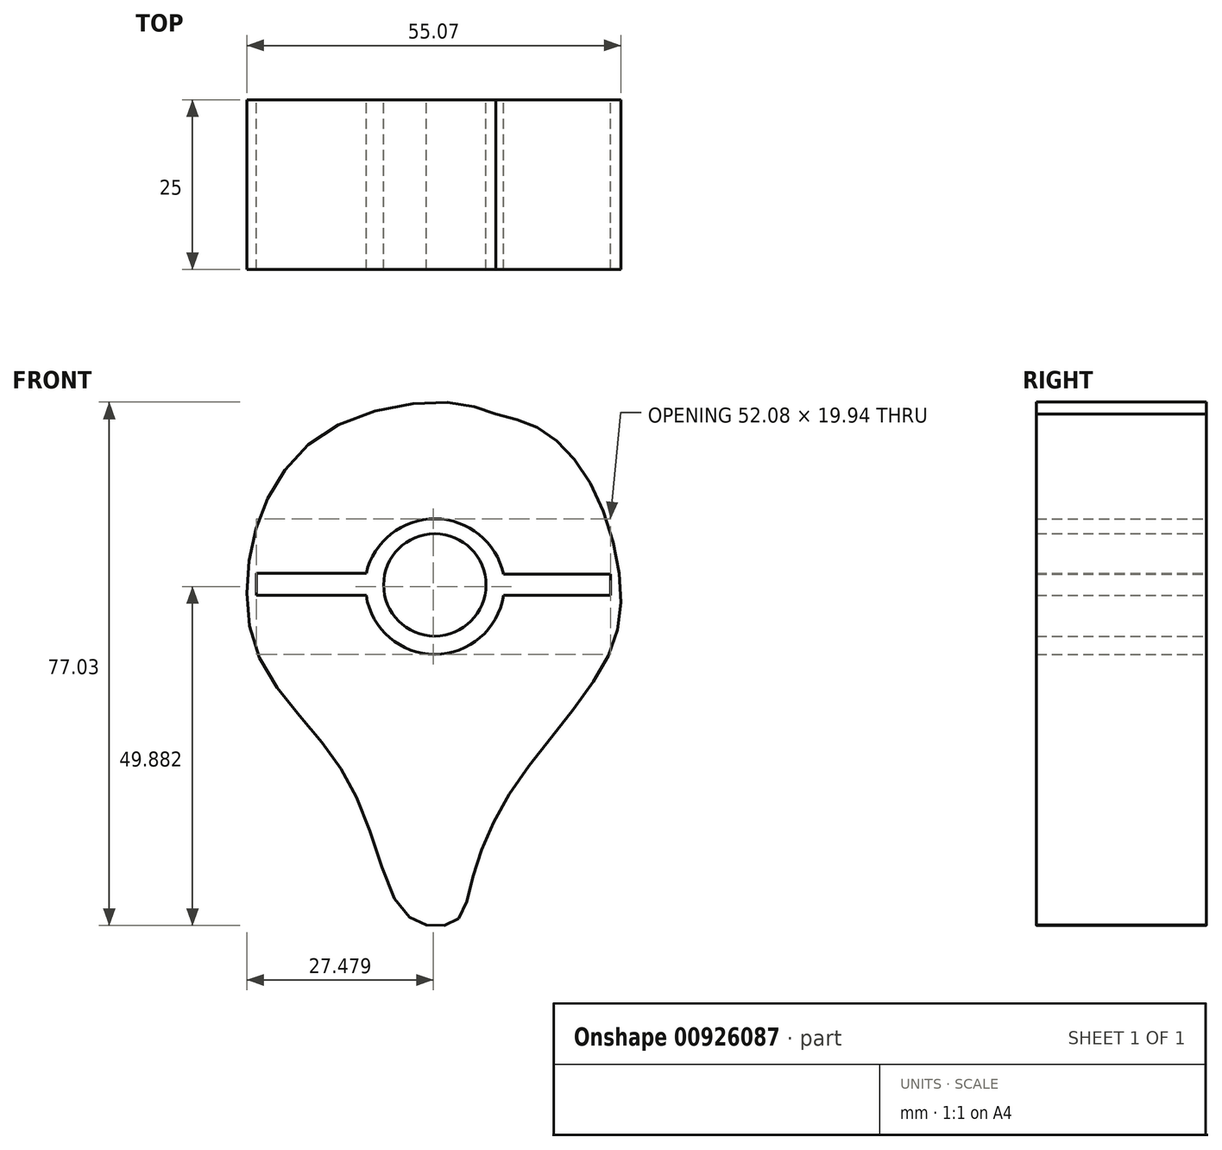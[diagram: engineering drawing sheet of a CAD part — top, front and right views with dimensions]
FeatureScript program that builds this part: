
annotation { "Feature Type Name" : "Feature", "Feature Type Description" : "" }
export const myFeature = defineFeature(function(context is Context, id is Id, definition is map)
    precondition{}
    {
        {
            var Q0;
            Q0=qCreatedBy(makeId("Front.planeOp"),FACE);
            var sketch = newSketch(context, id + "F0", { "sketchPlane" : qUnion([Q0])});
            skPoint(sketch, "E0.5.internal.snap0", {"position": v(-20.94, -36.11) * mm});
            skPoint(sketch, "E1", {"position": v(-15.16, 42.84) * mm});
            skFitSpline(sketch, "E2", {"points": [v(-22.22, -34.04) * mm, v(-17.77, -33.44) * mm, v(-15.12, -26.1) * mm, v(-8.38, -12.38) * mm, v(3.29, 3.14) * mm, v(6.42, 14.82) * mm, v(2.42, 29.99) * mm, v(-4.78, 38.5) * mm, v(-11.98, 41.11) * mm], "startDerivative": vector(63.97, -5.68) * mm, "endDerivative": vector(-71.35, 17.19) * mm});
            skFitSpline(sketch, "E3", {"points": [v(-11.98, 41.11) * mm, v(-19.18, 42.84) * mm, v(-35.38, 39.45) * mm, v(-45.14, 29.5) * mm, v(-48.52, 17.49) * mm, v(-46.64, 4.91) * mm, v(-37.82, -6.9) * mm, v(-31.25, -18.17) * mm, v(-26, -31.68) * mm, v(-22.22, -34.04) * mm], "startDerivative": vector(-71.1, 26.44) * mm, "endDerivative": vector(58.2, -19.36) * mm});
            skLineSegment(sketch, "E4", {"start": v(-47.2, 14.41) * mm, "end": v(-31.06, 14.41) * mm});
            skLineSegment(sketch, "E5", {"start": v(-31.06, 17.7) * mm, "end": v(-47.2, 17.7) * mm});
            skLineSegment(sketch, "E6", {"start": v(-10.86, 14.41) * mm, "end": v(4.88, 14.41) * mm});
            skLineSegment(sketch, "E7", {"start": v(4.88, 17.56) * mm, "end": v(-10.86, 17.56) * mm});
            skArc(sketch, "E8", {"start": v(-10.86, 17.56) * mm, "mid": v(-20.91, 25.7) * mm, "end": v(-31.06, 17.7) * mm});
            skArc(sketch, "E9", {"start": v(-31.06, 14.41) * mm, "mid": v(-20.96, 5.75) * mm, "end": v(-10.86, 14.41) * mm});
            skCircle(sketch, "E10", {"center": v(-20.96, 15.97) * mm, "radius": 7.53 * mm});
            skLineSegment(sketch, "E11", {"start": v(-47.2, 17.7) * mm, "end": v(-47.2, 14.41) * mm});
            skLineSegment(sketch, "E12", {"start": v(4.88, 17.56) * mm, "end": v(4.88, 14.41) * mm});
            skSolve(sketch);
        }
        {
            var Q0;
            Q0 = qSketchRegion(id + "F0", true);
            var Q1;
            Q1=makeQuery(id+"F0.imprint","IMPRINT",FACE,{"disambiguationData":[TD([[makeQuery(id+"F0.imprint","IMPRINT",EDGE,{"derivedFrom":sQuery(id+"F0.wireOp",EDGE,"E10")}),1.0]])]});
            extrude(context, id + "F1", {"entities" : qUnion([Q0, Q1]), "depth" : 25 * mm, "offsetDistance" : 25 * mm});
        }
    });
